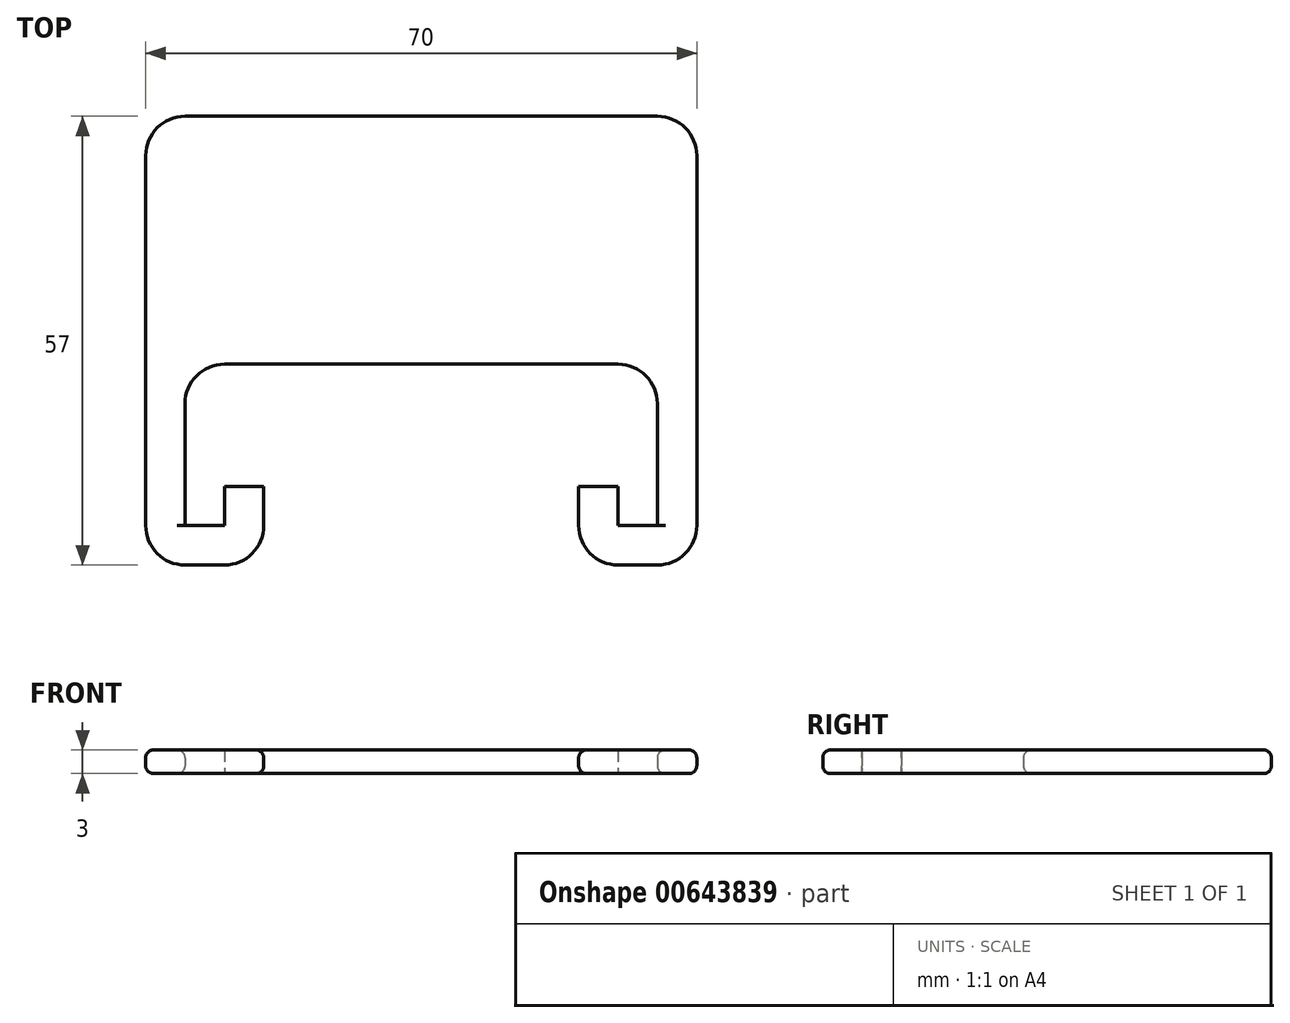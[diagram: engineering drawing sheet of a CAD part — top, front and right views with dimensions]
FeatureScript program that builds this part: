
annotation { "Feature Type Name" : "Feature", "Feature Type Description" : "" }
export const myFeature = defineFeature(function(context is Context, id is Id, definition is map)
    precondition{}
    {
        {
            var Q0;
            Q0=qCreatedBy(makeId("Top.planeOp"),FACE);
            var sketch = newSketch(context, id + "F0", { "sketchPlane" : qUnion([Q0])});
            skLineSegment(sketch, "E0.bottom", {"start": v(35, 22.5) * mm, "end": v(-35, 22.5) * mm});
            skLineSegment(sketch, "E0.left", {"start": v(35, 22.5) * mm, "end": v(35, -22.5) * mm});
            skLineSegment(sketch, "E0.right", {"start": v(-35, 22.5) * mm, "end": v(-35, -22.5) * mm});
            skPoint(sketch, "E0.middle", {"position": v(0, 0) * mm});
            skLineSegment(sketch, "E1", {"start": v(35, -22.5) * mm, "end": v(35, -34.5) * mm});
            skLineSegment(sketch, "E2", {"start": v(35, -34.5) * mm, "end": v(20, -34.5) * mm});
            skLineSegment(sketch, "E3", {"start": v(20, -34.5) * mm, "end": v(20, -24.5) * mm});
            skLineSegment(sketch, "E4", {"start": v(20, -24.5) * mm, "end": v(25, -24.5) * mm});
            skLineSegment(sketch, "E5", {"start": v(25, -24.5) * mm, "end": v(25, -29.5) * mm});
            skLineSegment(sketch, "E6", {"start": v(25, -29.5) * mm, "end": v(30, -29.5) * mm});
            skLineSegment(sketch, "E7", {"start": v(30, -29.5) * mm, "end": v(30, -9) * mm});
            skLineSegment(sketch, "E8.MirrorCS", {"start": v(-20, -34.5) * mm, "end": v(-20, -24.5) * mm});
            skLineSegment(sketch, "E9.MirrorCS", {"start": v(-20, -24.5) * mm, "end": v(-25, -24.5) * mm});
            skLineSegment(sketch, "E10.MirrorCS", {"start": v(-25, -24.5) * mm, "end": v(-25, -29.5) * mm});
            skLineSegment(sketch, "E11.MirrorCS", {"start": v(-25, -29.5) * mm, "end": v(-30, -29.5) * mm});
            skLineSegment(sketch, "E12.MirrorCS", {"start": v(-35, -34.5) * mm, "end": v(-20, -34.5) * mm});
            skLineSegment(sketch, "E13.MirrorCS", {"start": v(-35, -22.5) * mm, "end": v(-35, -34.5) * mm});
            skLineSegment(sketch, "E14.MirrorCS", {"start": v(-30, -29.5) * mm, "end": v(-30, -9) * mm});
            skLineSegment(sketch, "E15", {"start": v(-30, -9) * mm, "end": v(30, -9) * mm});
            skSolve(sketch);
        }
        {
            var Q0;
            Q0 = qSketchRegion(id + "F0", true);
            extrude(context, id + "F1", {"entities" : qUnion([Q0]), "depth" : 3 * mm, "offsetDistance" : 25 * mm});
        }
        {
            var Q0;
            Q0=makeQuery(id+"F1.opExtrude","SWEPT_EDGE",EDGE,{"disambiguationData":[OSD([sQuery(id+"F0.wireOp",EDGE,"E12.MirrorCS"),sQuery(id+"F0.wireOp",EDGE,"E13.MirrorCS")])]});
            var Q1;
            Q1=makeQuery(id+"F1.opExtrude","SWEPT_EDGE",EDGE,{"disambiguationData":[OSD([sQuery(id+"F0.wireOp",EDGE,"E8.MirrorCS"),sQuery(id+"F0.wireOp",EDGE,"E12.MirrorCS")])]});
            var Q2;
            Q2=makeQuery(id+"F1.opExtrude","SWEPT_EDGE",EDGE,{"disambiguationData":[OSD([sQuery(id+"F0.wireOp",EDGE,"E14.MirrorCS"),sQuery(id+"F0.wireOp",EDGE,"E15")])]});
            var Q3;
            Q3=makeQuery(id+"F1.opExtrude","SWEPT_EDGE",EDGE,{"disambiguationData":[OSD([sQuery(id+"F0.wireOp",EDGE,"E1"),sQuery(id+"F0.wireOp",EDGE,"E2")])]});
            var Q4;
            Q4=makeQuery(id+"F1.opExtrude","SWEPT_EDGE",EDGE,{"disambiguationData":[OSD([sQuery(id+"F0.wireOp",EDGE,"E2"),sQuery(id+"F0.wireOp",EDGE,"E3")])]});
            var Q5;
            Q5=makeQuery(id+"F1.opExtrude","SWEPT_EDGE",EDGE,{"disambiguationData":[OSD([sQuery(id+"F0.wireOp",EDGE,"E0.bottom"),sQuery(id+"F0.wireOp",EDGE,"E0.left")])]});
            var Q6;
            Q6=makeQuery(id+"F1.opExtrude","SWEPT_EDGE",EDGE,{"disambiguationData":[OSD([sQuery(id+"F0.wireOp",EDGE,"E0.bottom"),sQuery(id+"F0.wireOp",EDGE,"E0.right")])]});
            var Q7;
            Q7=makeQuery(id+"F1.opExtrude","SWEPT_EDGE",EDGE,{"disambiguationData":[OSD([sQuery(id+"F0.wireOp",EDGE,"E7"),sQuery(id+"F0.wireOp",EDGE,"E15")])]});
            fillet(context, id + "F2", {"entities" : qUnion([Q0, Q1, Q2, Q3, Q4, Q5, Q6, Q7]), "radius" : 5 * mm, "tangentPropagation" : true, "allowEdgeOverflow" : false});
        }
        {
            var Q0;
            Q0=makeQuery(id+"F1.opExtrude","CAP_EDGE",EDGE,{"disambiguationData":[OSD([sQuery(id+"F0.wireOp",EDGE,"E0.bottom")])],"isStart":false});
            var Q1;
            Q1=makeQuery(id+"F1.opExtrude","CAP_EDGE",EDGE,{"disambiguationData":[OSD([sQuery(id+"F0.wireOp",EDGE,"E0.bottom")])],"isStart":true});
            var Q2;
            Q2=makeQuery(id+"F1.opExtrude","CAP_EDGE",EDGE,{"disambiguationData":[OSD([sQuery(id+"F0.wireOp",EDGE,"E15")])],"isStart":false});
            var Q3;
            Q3=makeQuery(id+"F1.opExtrude","CAP_EDGE",EDGE,{"disambiguationData":[OSD([sQuery(id+"F0.wireOp",EDGE,"E7")])],"isStart":false});
            var Q4;
            Q4=makeQuery(id+"F1.opExtrude","CAP_EDGE",EDGE,{"disambiguationData":[OSD([sQuery(id+"F0.wireOp",EDGE,"E15")])],"isStart":true});
            var Q5;
            Q5=makeQuery(id+"F1.opExtrude","CAP_EDGE",EDGE,{"disambiguationData":[OSD([sQuery(id+"F0.wireOp",EDGE,"E7")])],"isStart":true});
            fillet(context, id + "F3", {"entities" : qUnion([Q0, Q1, Q2, Q3, Q4, Q5]), "radius" : 1 * mm, "tangentPropagation" : true, "allowEdgeOverflow" : false});
        }
    });
